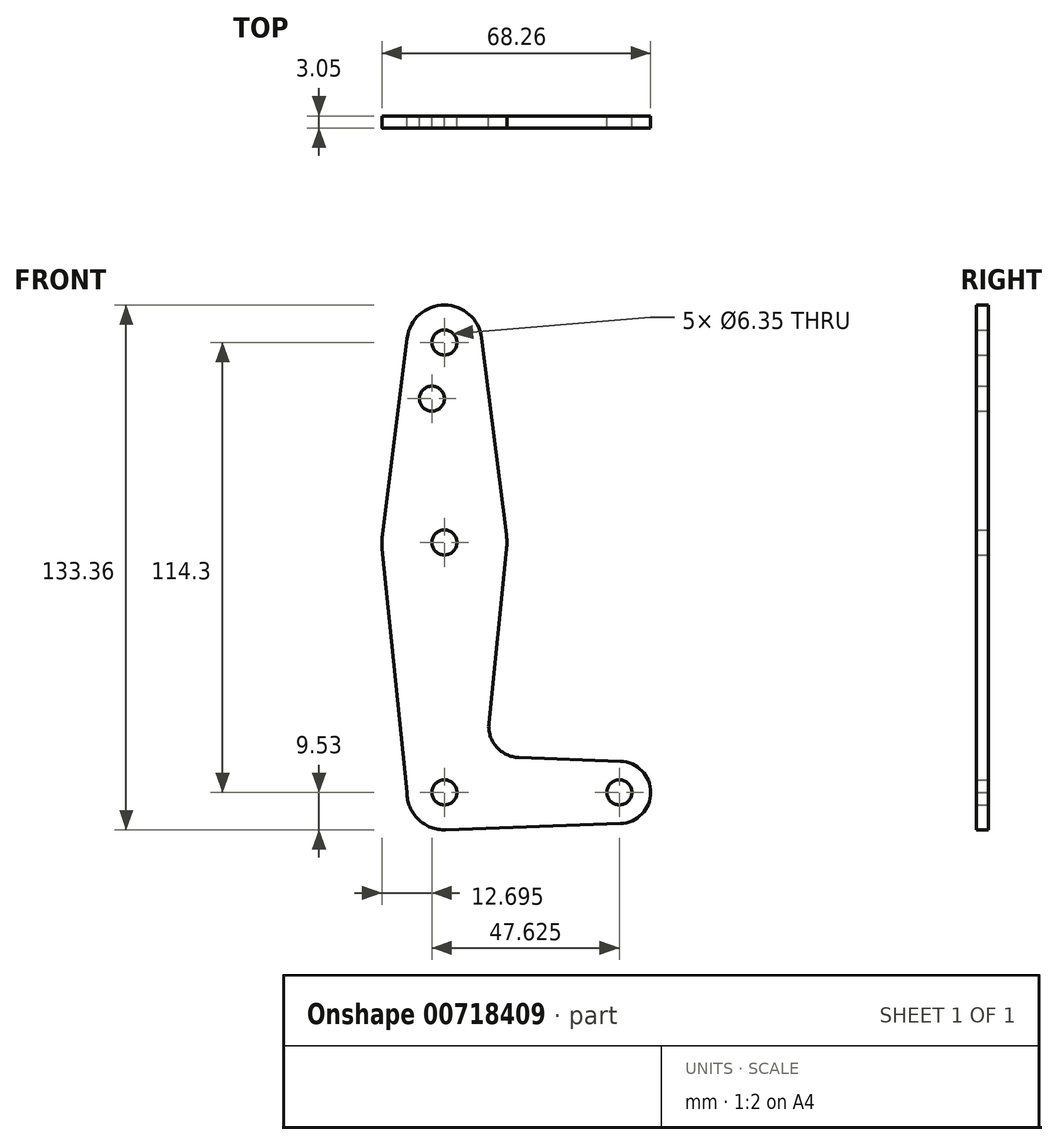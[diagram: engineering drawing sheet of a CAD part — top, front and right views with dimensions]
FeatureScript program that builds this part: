
annotation { "Feature Type Name" : "Feature", "Feature Type Description" : "" }
export const myFeature = defineFeature(function(context is Context, id is Id, definition is map)
    precondition{}
    {
        {
            var Q0;
            Q0=qCreatedBy(makeId("Front.planeOp"),FACE);
            var sketch = newSketch(context, id + "F0", { "sketchPlane" : qUnion([Q0])});
            skArc(sketch, "E0", {"start": v(0.34, 9.52) * mm, "mid": v(0.17, 9.52) * mm, "end": v(0, 9.52) * mm});
            skLineSegment(sketch, "E1", {"start": v(0, 0) * mm, "end": v(0, 63.5) * mm, "construction": true});
            skCircle(sketch, "E2", {"center": v(0, 114.3) * mm, "radius": 9.53 * mm});
            skLineSegment(sketch, "E3", {"start": v(0, 0) * mm, "end": v(44.45, 0) * mm, "construction": true});
            skCircle(sketch, "E4", {"center": v(44.45, 0) * mm, "radius": 7.94 * mm});
            skCircle(sketch, "E5", {"center": v(0, 63.5) * mm, "radius": 15.88 * mm});
            skCircle(sketch, "E6", {"center": v(0, 114.3) * mm, "radius": 3.18 * mm});
            skCircle(sketch, "E7", {"center": v(0, 0) * mm, "radius": 3.18 * mm});
            skCircle(sketch, "E8", {"center": v(44.45, 0) * mm, "radius": 3.18 * mm});
            skPoint(sketch, "E9.newPointA", {"position": v(0, 9.53) * mm});
            skPoint(sketch, "E9.newPointB", {"position": v(9.57, 0) * mm});
            skCircle(sketch, "E10", {"center": v(-3.18, 100.03) * mm, "radius": 3.18 * mm});
            skCircle(sketch, "E11", {"center": v(0, 63.5) * mm, "radius": 3.18 * mm});
            skLineSegment(sketch, "E12", {"start": v(9.45, 115.5) * mm, "end": v(15.75, 65.48) * mm});
            skLineSegment(sketch, "E13", {"start": v(-9.45, 115.5) * mm, "end": v(-15.75, 65.48) * mm});
            skLineSegment(sketch, "E14", {"start": v(0, 114.3) * mm, "end": v(0, 63.5) * mm, "construction": true});
            skCircle(sketch, "E15", {"center": v(0, 0) * mm, "radius": 9.53 * mm});
            skLineSegment(sketch, "E16", {"start": v(11.3, 17.6) * mm, "end": v(15.8, 61.91) * mm});
            skLineSegment(sketch, "E17", {"start": v(-9.53, 0) * mm, "end": v(-15.8, 61.91) * mm});
            skLineSegment(sketch, "E18", {"start": v(44.73, 7.93) * mm, "end": v(18.93, 8.85) * mm});
            skLineSegment(sketch, "E19", {"start": v(44.73, -7.93) * mm, "end": v(0, -9.53) * mm});
            skPoint(sketch, "E20.start.orphan", {"position": v(44.45, -1.46) * mm});
            skArc(sketch, "E21.filletArc", {"start": v(11.3, 17.6) * mm, "mid": v(13.22, 11.57) * mm, "end": v(18.93, 8.85) * mm});
            skSolve(sketch);
        }
        {
            var Q0;
            {var subQ4=sQuery(id+"F0.wireOp",EDGE,"E16");Q0=makeQuery(id+"F0.imprint","IMPRINT",FACE,{"disambiguationData":[TD([[makeQuery(id+"F0.imprint","IMPRINT",EDGE,{"derivedFrom":subQ4}),1.0]])]});}
            var Q1;
            Q1=makeQuery(id+"F0.imprint","IMPRINT",FACE,{"disambiguationData":[TD([[makeQuery(id+"F0.imprint","IMPRINT",EDGE,{"derivedFrom":sQuery(id+"F0.wireOp",EDGE,"E11")}),-1.0]])]});
            var Q2;
            Q2=makeQuery(id+"F0.imprint","IMPRINT",FACE,{"disambiguationData":[TD([[makeQuery(id+"F0.imprint","IMPRINT",EDGE,{"derivedFrom":sQuery(id+"F0.wireOp",EDGE,"E10")}),-1.0]])]});
            var Q3;
            Q3=makeQuery(id+"F0.imprint","IMPRINT",FACE,{"disambiguationData":[TD([[makeQuery(id+"F0.imprint","IMPRINT",EDGE,{"derivedFrom":sQuery(id+"F0.wireOp",EDGE,"E6")}),-1.0]])]});
            var Q4;
            Q4=makeQuery(id+"F0.imprint","IMPRINT",FACE,{"disambiguationData":[TD([[makeQuery(id+"F0.imprint","IMPRINT",EDGE,{"derivedFrom":sQuery(id+"F0.wireOp",EDGE,"E7")}),-1.0]])]});
            var Q5;
            Q5=makeQuery(id+"F0.imprint","IMPRINT",FACE,{"disambiguationData":[TD([[makeQuery(id+"F0.imprint","IMPRINT",EDGE,{"derivedFrom":sQuery(id+"F0.wireOp",EDGE,"E8")}),-1.0]])]});
            extrude(context, id + "F1", {"entities" : qUnion([Q0, Q1, Q2, Q3, Q4, Q5]), "depth" : 3.05 * mm, "offsetDistance" : 25.4 * mm});
        }
    });
